FREECAD ASSEMBLY — COMPONENT RECIPES ("FlexureAssembly")

This assembly document has 7 components, labeled P0..P6 below (a component is one placed body or linked part). 6 of them carry a construction recipe — the FreeCAD feature program that regenerates the part from scratch, quoted from this document or its linked companion documents; the rest are supplied as boundary geometry only. No exploded tour is included for this assembly.
COMPONENT P0 — recipe-attached ("FlexureStiffener2", a linked part whose construction recipe lives in a companion FreeCAD document of the same project; that document's serialized recipe follows).
Construction recipe (the companion document, serialized — sketch geometry with constraints, then the solid features built on it; lengths are millimeters unless a unit is written):

FCSTD DOCUMENT  (FreeCAD 1.1R41365 (Git))
Label: FlexureStiffener
License: All rights reserved
LicenseURL: https://en.wikipedia.org/wiki/All_rights_reserved
objects: App::Point×1, Sketcher::SketchObject×1, PartDesign::Pad×1, PartDesign::Fillet×1, PartDesign::Body×1
note: 9 computed .brp shape members not serialized (recipe doc carries the construction recipe); baked Part::Feature solids carry a one-line shape summary decoded from their .brp

FEATURE [App::Point] Origin001
  Role = Origin
FEATURE [Sketcher::SketchObject] Sketch
  ArcFitTolerance = 1e-06
  AttachmentSupport = -> [XZ_Plane]
  ExternalTypes = [0]
  FullyConstrained = true
  MakeInternals = false
  MapMode = 5
  Placement = pos=(0,0,0) rot=(1,0,0;1.5708rad)
  sketch-geometry (14):
    g0: LineSegment StartX=0.669696 StartY=1.61679 StartZ=0 EndX=-0.669696 EndY=1.61679 EndZ=0
    g1: LineSegment StartX=-0.669696 StartY=1.61679 StartZ=0 EndX=-1.61679 EndY=0.669696 EndZ=0
    g2: LineSegment StartX=-1.61679 StartY=0.669696 StartZ=0 EndX=-1.61679 EndY=-0.669696 EndZ=0
    g3: LineSegment StartX=-1.61679 StartY=-0.669696 StartZ=0 EndX=-0.669696 EndY=-1.61679 EndZ=0
    g4: LineSegment StartX=-0.669696 StartY=-1.61679 StartZ=0 EndX=0.669696 EndY=-1.61679 EndZ=0
    g5: LineSegment StartX=0.669696 StartY=-1.61679 StartZ=0 EndX=1.61679 EndY=-0.669696 EndZ=0
    g6: LineSegment StartX=1.61679 StartY=-0.669696 StartZ=0 EndX=1.61679 EndY=0.669696 EndZ=0
    g7: LineSegment StartX=1.61679 StartY=0.669696 StartZ=0 EndX=0.669696 EndY=1.61679 EndZ=0
    g8: Circle [constr] CenterX=0 CenterY=0 CenterZ=0 NormalX=0 NormalY=0 NormalZ=1 AngleXU=0 Radius=1.75
    g9: LineSegment StartX=-0.3 StartY=-0.325 StartZ=0 EndX=0.3 EndY=-0.325 EndZ=0
    g10: LineSegment StartX=0.3 StartY=-0.325 StartZ=0 EndX=0.3 EndY=0.325 EndZ=0
    g11: LineSegment StartX=0.3 StartY=0.325 StartZ=0 EndX=-0.3 EndY=0.325 EndZ=0
    g12: LineSegment StartX=-0.3 StartY=0.325 StartZ=0 EndX=-0.3 EndY=-0.325 EndZ=0
    g13: GeomPoint [constr] X=0 Y=0 Z=0
  constraints (32):
    c: Coincident(g0,g1)
    c: Coincident(g1,g2)
    c: Coincident(g2,g3)
    c: Coincident(g3,g4)
    c: Coincident(g4,g5)
    c: Coincident(g5,g6)
    c: Coincident(g6,g7)
    c: Coincident(g7,g0)
    c: Equal(g0, g1-g7) x7
    c: PointOnObject(g0,g8)
    c: PointOnObject(g1,g8)
    c: PointOnObject(g2,g8)
    c: PointOnObject(g3,g8)
    c: PointOnObject(g4,g8)
    c: PointOnObject(g5,g8)
    c: PointOnObject(g6,g8)
    c: PointOnObject(g7,g8)
    c: Coincident(g8,g-1)
    c: Vertical(g6)
    c: Diameter(g8) = 3.5
    c: Coincident(g9,g10)
    c: Coincident(g10,g11)
    c: Coincident(g11,g12)
    c: Coincident(g12,g9)
    c: Horizontal(g9)
    c: Horizontal(g11)
    c: Vertical(g10)
    c: Vertical(g12)
    c: Symmetric(g11,g9,g13)
    c: Coincident(g13,g8)
    c: DistanceY(g10,g10) = 0.65
    c: DistanceX(g11,g11) = 0.6
FEATURE [PartDesign::Pad] Pad
  Direction = (0,-1,2e-16)
  Length = 40
  Length2 = 10
  Midplane = true
  Placement = pos=(0,0,0) rot=(1,0,0;1.5708rad)
  Profile = -> Sketch
  ReferenceAxis = -> Sketch [N_Axis]
  Refine = true
  Suppressed = false
  Type = 0
FEATURE [PartDesign::Fillet] Fillet
  Base = -> Pad [Edge5,Edge8,Edge20,Edge17]
  BaseFeature = -> Pad
  Placement = pos=(0,0,0) rot=(1,0,0;1.5708rad)
  Radius = 0.25
  Refine = true
  SupportTransform = false
  Suppressed = false
  UseAllEdges = false
FEATURE [PartDesign::Body] Body  label="FlexureStiffener"
  AllowCompound = false
  Group = -> [Sketch,Pad,Fillet]
  Origin = -> Origin
  Tip = -> Fillet
COMPONENT P1 — recipe-attached ("FlexureWire1", a linked part whose construction recipe lives in a companion FreeCAD document of the same project; that document's serialized recipe follows).
Construction recipe (the companion document, serialized — sketch geometry with constraints, then the solid features built on it; lengths are millimeters unless a unit is written):

FCSTD DOCUMENT  (FreeCAD 1.1R41365 (Git))
Label: FlexureWire
License: All rights reserved
LicenseURL: https://en.wikipedia.org/wiki/All_rights_reserved
objects: App::Point×1, Sketcher::SketchObject×1, PartDesign::Pad×1, PartDesign::Body×1
note: 6 computed .brp shape members not serialized (recipe doc carries the construction recipe); baked Part::Feature solids carry a one-line shape summary decoded from their .brp

FEATURE [App::Point] Origin001
  Role = Origin
FEATURE [Sketcher::SketchObject] Sketch
  ArcFitTolerance = 1e-06
  AttachmentSupport = -> [XZ_Plane]
  ExternalTypes = [0]
  FullyConstrained = true
  MakeInternals = false
  MapMode = 5
  Placement = pos=(0,0,0) rot=(1,0,0;1.5708rad)
  sketch-geometry (1):
    g0: Circle CenterX=0 CenterY=0 CenterZ=0 NormalX=0 NormalY=0 NormalZ=1 AngleXU=0 Radius=0.25
  constraints (2):
    c: Coincident(g0,g-1)
    c: Diameter(g0) = 0.5
FEATURE [PartDesign::Pad] Pad
  Direction = (0,-1,0)
  Length = 62
  Length2 = 10
  Placement = pos=(0,0,0) rot=(1,0,0;1.5708rad)
  Profile = -> Sketch
  ReferenceAxis = -> Sketch [N_Axis]
  Refine = true
  Suppressed = false
  Type = 0
FEATURE [PartDesign::Body] Body  label="FlexureWire"
  AllowCompound = false
  Group = -> [Sketch,Pad]
  Origin = -> Origin
  Tip = -> Pad
COMPONENT P2 — same part as P1; its construction recipe is shown at P1.
COMPONENT P3 — same part as P0; its construction recipe is shown at P0.
COMPONENT P4 — recipe-attached ("WireMount1", a linked part whose construction recipe lives in a companion FreeCAD document of the same project; that document's serialized recipe follows).
Construction recipe (the companion document, serialized — sketch geometry with constraints, then the solid features built on it; lengths are millimeters unless a unit is written):

FCSTD DOCUMENT  (FreeCAD 1.1R41365 (Git))
Label: WireMount
License: All rights reserved
LicenseURL: https://en.wikipedia.org/wiki/All_rights_reserved
objects: Sketcher::SketchObject×3, PartDesign::Pocket×2, PartDesign::Chamfer×2, App::Point×1, PartDesign::Pad×1, PartDesign::Fillet×1, PartDesign::Mirrored×1, PartDesign::Body×1
note: 27 computed .brp shape members not serialized (recipe doc carries the construction recipe); baked Part::Feature solids carry a one-line shape summary decoded from their .brp

FEATURE [App::Point] Origin001
  Role = Origin
FEATURE [Sketcher::SketchObject] Sketch
  ArcFitTolerance = 1e-06
  AttachmentSupport = -> [XY_Plane]
  ExternalTypes = [0]
  FullyConstrained = true
  MakeInternals = false
  MapMode = 5
  sketch-geometry (5):
    g0: LineSegment StartX=-10 StartY=-2.75 StartZ=0 EndX=0 EndY=-2.75 EndZ=0
    g1: LineSegment StartX=0 StartY=-2.75 StartZ=0 EndX=0 EndY=2.75 EndZ=0
    g2: LineSegment StartX=0 StartY=2.75 StartZ=0 EndX=-10 EndY=2.75 EndZ=0
    g3: LineSegment StartX=-10 StartY=2.75 StartZ=0 EndX=-10 EndY=-2.75 EndZ=0
    g4: GeomPoint [constr] X=0 Y=0 Z=0
  constraints (12):
    c: Coincident(g0,g1)
    c: Coincident(g1,g2)
    c: Coincident(g2,g3)
    c: Coincident(g3,g0)
    c: Horizontal(g0)
    c: Horizontal(g2)
    c: Vertical(g1)
    c: Vertical(g3)
    c: Coincident(g4,g-1)
    c: DistanceX(g0,g0) = 10
    c: DistanceY(g1,g1) = 5.5
    c: Symmetric(g1,g1,g4)
FEATURE [PartDesign::Pad] Pad
  Direction = (0,0,1)
  Length = 3
  Length2 = 10
  Profile = -> Sketch
  ReferenceAxis = -> Sketch [N_Axis]
  Refine = true
  Suppressed = false
  Type = 0
FEATURE [Sketcher::SketchObject] Sketch001
  ArcFitTolerance = 1e-06
  AttachmentSupport = -> [Pad]
  ExternalTypes = [0]
  FullyConstrained = true
  MakeInternals = false
  MapMode = 5
  Placement = pos=(0,0,3) rot=(0,0,1;0rad)
  sketch-geometry (1):
    g0: Circle CenterX=-6 CenterY=0 CenterZ=0 NormalX=0 NormalY=0 NormalZ=1 AngleXU=0 Radius=1.1
  constraints (3):
    c: Diameter(g0) = 2.2
    c: DistanceX(g0,g-1) = 6
    c: PointOnObject(g0,g-1)
FEATURE [PartDesign::Pocket] Pocket
  BaseFeature = -> Pad
  Direction = (0,0,-1)
  Length = 5
  Length2 = 5
  Profile = -> Sketch001
  ReferenceAxis = -> Sketch001 [N_Axis]
  Refine = true
  Suppressed = false
  Type = 1
FEATURE [Sketcher::SketchObject] Sketch002
  ArcFitTolerance = 1e-06
  AttachmentSupport = -> [Pocket]
  ExternalTypes = [0]
  FullyConstrained = true
  MakeInternals = false
  MapMode = 5
  Placement = pos=(0,-2.75,0) rot=(1,0,0;1.5708rad)
  sketch-geometry (5):
    g0: LineSegment StartX=-8.3 StartY=1.2 StartZ=0 EndX=-7.7 EndY=1.2 EndZ=0
    g1: LineSegment StartX=-7.7 StartY=1.2 StartZ=0 EndX=-7.7 EndY=1.8 EndZ=0
    g2: LineSegment StartX=-7.7 StartY=1.8 StartZ=0 EndX=-8.3 EndY=1.8 EndZ=0
    g3: LineSegment StartX=-8.3 StartY=1.8 StartZ=0 EndX=-8.3 EndY=1.2 EndZ=0
    g4: GeomPoint [constr] X=-8 Y=1.5 Z=0
  constraints (13):
    c: Coincident(g0,g1)
    c: Coincident(g1,g2)
    c: Coincident(g2,g3)
    c: Coincident(g3,g0)
    c: Horizontal(g0)
    c: Horizontal(g2)
    c: Vertical(g1)
    c: Vertical(g3)
    c: Symmetric(g2,g0,g4)
    c: DistanceY(g3,g3) = 0.6
    c: DistanceX(g0,g0) = 0.6
    c: DistanceY(g-1,g4) = 1.5
    c: DistanceX(g4,g-1) = 8
FEATURE [PartDesign::Pocket] Pocket001
  BaseFeature = -> Pocket
  Direction = (0,1,-2e-16)
  Length = 5
  Length2 = 5
  Profile = -> Sketch002
  ReferenceAxis = -> Sketch002 [N_Axis]
  Refine = true
  Suppressed = false
  Type = 1
FEATURE [PartDesign::Fillet] Fillet
  Base = -> Pocket001 [Edge1,Edge9]
  BaseFeature = -> Pocket001
  Radius = 0.75
  Refine = true
  SupportTransform = false
  Suppressed = false
  UseAllEdges = false
FEATURE [PartDesign::Mirrored] Mirrored
  BaseFeature = -> Fillet
  MirrorPlane = -> YZ_Plane
  Refine = true
  Suppressed = false
  TransformMode = 1
FEATURE [PartDesign::Chamfer] Chamfer
  Angle = 45
  Base = -> Mirrored [Edge50,Edge52]
  BaseFeature = -> Mirrored
  ChamferType = 0
  FlipDirection = false
  Refine = true
  Size = 1.2
  Size2 = 1
  SupportTransform = false
  Suppressed = false
  UseAllEdges = false
FEATURE [PartDesign::Chamfer] Chamfer001
  Angle = 45
  Base = -> Chamfer [Edge6]
  BaseFeature = -> Chamfer
  ChamferType = 0
  FlipDirection = false
  Refine = true
  Size = 0.4
  Size2 = 1
  SupportTransform = false
  Suppressed = false
  UseAllEdges = false
FEATURE [PartDesign::Body] Body  label="WireMount"
  AllowCompound = false
  Group = -> [Sketch,Pad,Sketch001,Pocket,Sketch002,Pocket001,Fillet,Mirrored,Chamfer,Chamfer001]
  Origin = -> Origin
  Tip = -> Chamfer001
COMPONENT P5 — same part as P4; its construction recipe is shown at P4.
COMPONENT P6 — geometry summary ("WireMountFixture"; no construction recipe available for this part):
  bounding box: 70.0 x 25.0 x 6.0 mm
  tessellated surface: 8,106 triangles
  volume: 5757 mm^3 (55% of its bounding box)
PROVENANCE & LICENSES
A FreeCAD (.FCStd) document from a public repository crawl; recipes are the document's own serialized feature recipes (and, for linked parts, companion documents' recipes).
License: mit.
